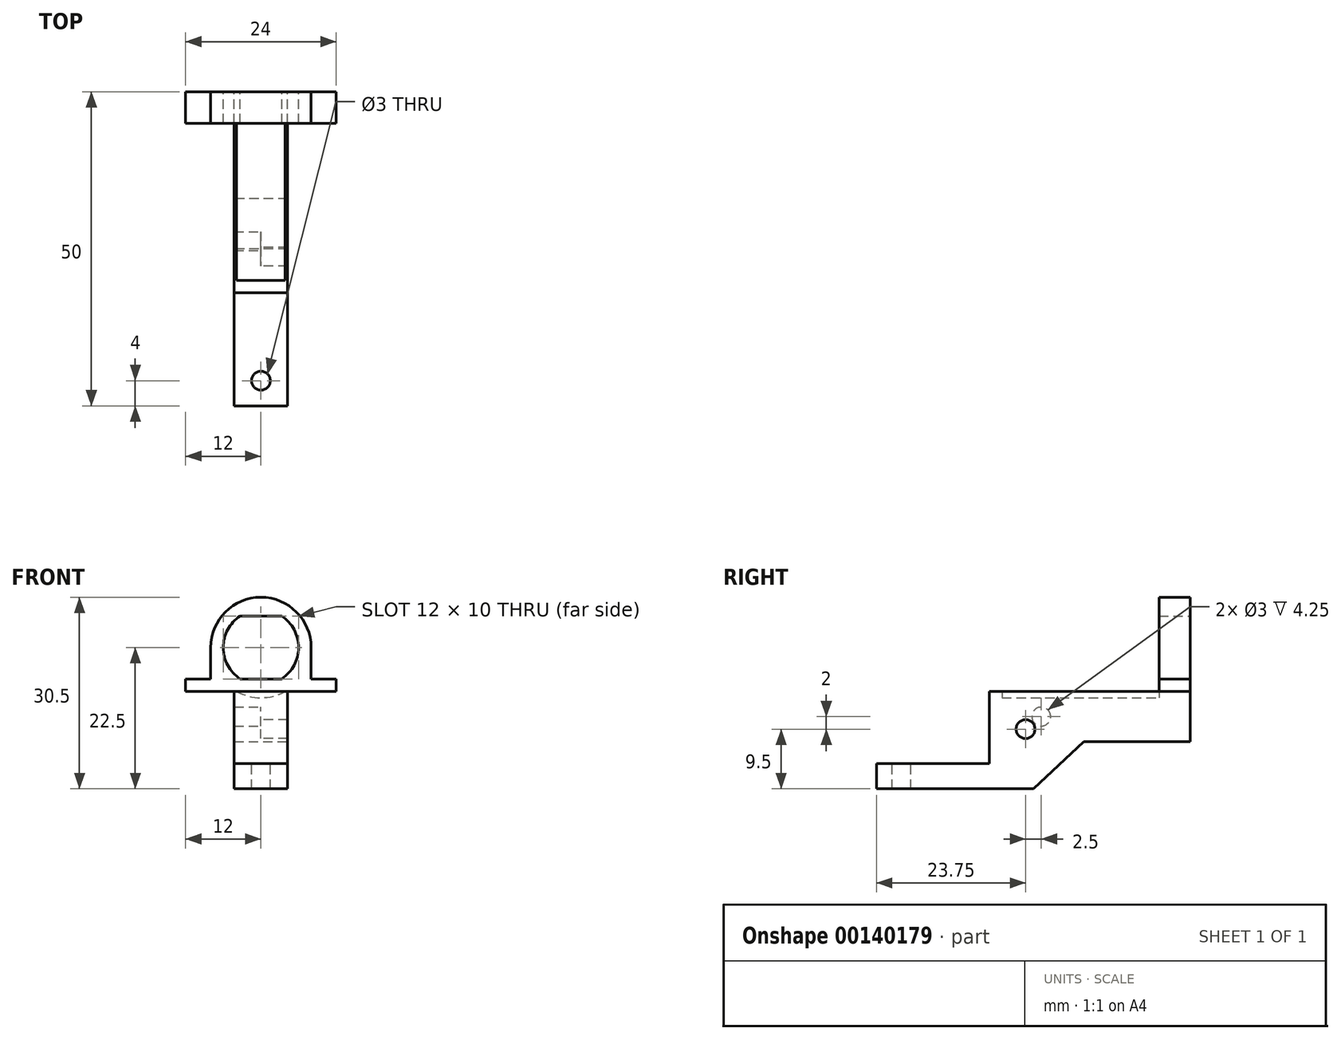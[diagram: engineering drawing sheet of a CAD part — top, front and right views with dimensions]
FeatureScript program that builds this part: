
annotation { "Feature Type Name" : "Feature", "Feature Type Description" : "" }
export const myFeature = defineFeature(function(context is Context, id is Id, definition is map)
    precondition{}
    {
        {
            var Q0;
            Q0=qCreatedBy(makeId("Front.planeOp"),FACE);
            var sketch = newSketch(context, id + "F0", { "sketchPlane" : qUnion([Q0])});
            skArc(sketch, "E0", {"start": v(3.32, 2) * mm, "mid": v(6, 7) * mm, "end": v(3.32, 12) * mm});
            skLineSegment(sketch, "E1", {"start": v(-3.32, 12) * mm, "end": v(3.32, 12) * mm});
            skLineSegment(sketch, "E2", {"start": v(-3.32, 2) * mm, "end": v(3.32, 2) * mm});
            skLineSegment(sketch, "E3", {"start": v(-8, 2) * mm, "end": v(-12, 2) * mm});
            skLineSegment(sketch, "E4", {"start": v(-12, 2) * mm, "end": v(-12, 0) * mm});
            skLineSegment(sketch, "E5", {"start": v(-12, 0) * mm, "end": v(0, 0) * mm});
            skArc(sketch, "E6.trimOffspring", {"start": v(-3.32, 12) * mm, "mid": v(-6, 7) * mm, "end": v(-3.32, 2) * mm});
            skArc(sketch, "E7", {"start": v(8, 7) * mm, "mid": v(0, 15) * mm, "end": v(-8, 7) * mm});
            skLineSegment(sketch, "E8", {"start": v(-8, 7) * mm, "end": v(-8, 2) * mm});
            skLineSegment(sketch, "E9.MirrorCS", {"start": v(8, 7) * mm, "end": v(8, 2) * mm});
            skLineSegment(sketch, "E10.MirrorCS", {"start": v(8, 2) * mm, "end": v(12, 2) * mm});
            skLineSegment(sketch, "E11.MirrorCS", {"start": v(12, 2) * mm, "end": v(12, 0) * mm});
            skLineSegment(sketch, "E12.MirrorCS", {"start": v(12, 0) * mm, "end": v(0, 0) * mm});
            skLineSegment(sketch, "E13.bottom", {"start": v(-4.25, 0) * mm, "end": v(4.25, 0) * mm});
            skLineSegment(sketch, "E13.top", {"start": v(-4.25, -8) * mm, "end": v(4.25, -8) * mm});
            skLineSegment(sketch, "E13.left", {"start": v(-4.25, 0) * mm, "end": v(-4.25, -8) * mm});
            skLineSegment(sketch, "E13.right", {"start": v(4.25, 0) * mm, "end": v(4.25, -8) * mm});
            skSolve(sketch);
        }
        {
            var Q0;
            Q0=makeQuery(id+"F0.imprint","IMPRINT",FACE,{"disambiguationData":[TD([[makeQuery(id+"F0.imprint","IMPRINT",EDGE,{"derivedFrom":sQuery(id+"F0.wireOp",EDGE,"E0")}),-1.0]])]});
            extrude(context, id + "F1", {"entities" : qUnion([Q0]), "depth" : 5 * mm});
        }
        {
            var Q0;
            Q0=makeQuery(id+"F0.imprint","IMPRINT",FACE,{"disambiguationData":[TD([[makeQuery(id+"F0.imprint","IMPRINT",EDGE,{"derivedFrom":sQuery(id+"F0.wireOp",EDGE,"E13.top")}),1.0]])]});
            extrude(context, id + "F2", {"entities" : qUnion([Q0]), "operationType" : NewBodyOperationType.ADD, "depth" : 32 * mm});
        }
        {
            var Q0;
            Q0=qCreatedBy(makeId("Right.planeOp"),FACE);
            var sketch = newSketch(context, id + "F3", { "sketchPlane" : qUnion([Q0])});
            skCircle(sketch, "E14", {"center": v(-26.25, -6) * mm, "radius": 1.5 * mm});
            skCircle(sketch, "E15", {"center": v(-23.75, -4) * mm, "radius": 1.5 * mm});
            skSolve(sketch);
        }
        {
            var Q0;
            Q0=makeQuery(id+"F3.imprint","IMPRINT",FACE,{"disambiguationData":[TD([[makeQuery(id+"F3.imprint","IMPRINT",EDGE,{"derivedFrom":sQuery(id+"F3.wireOp",EDGE,"E15")}),1.0]])]});
            extrude(context, id + "F4", {"entities" : qUnion([Q0]), "operationType" : NewBodyOperationType.REMOVE, "oppositeDirection" : true, "depth" : 25 * mm});
        }
        {
            var Q0;
            Q0=makeQuery(id+"F3.imprint","IMPRINT",FACE,{"disambiguationData":[TD([[makeQuery(id+"F3.imprint","IMPRINT",EDGE,{"derivedFrom":sQuery(id+"F3.wireOp",EDGE,"E14")}),1.0]])]});
            extrude(context, id + "F5", {"entities" : qUnion([Q0]), "operationType" : NewBodyOperationType.REMOVE, "depth" : 25 * mm});
        }
        {
            var Q0;
            Q0=makeQuery(id+"F1.opExtrude","CAP_FACE",FACE,{"disambiguationData":[OSD([sQuery(id+"F0.wireOp",EDGE,"E0"),sQuery(id+"F0.wireOp",EDGE,"E1"),sQuery(id+"F0.wireOp",EDGE,"E2"),sQuery(id+"F0.wireOp",EDGE,"E3"),sQuery(id+"F0.wireOp",EDGE,"E4"),sQuery(id+"F0.wireOp",EDGE,"E5"),sQuery(id+"F0.wireOp",EDGE,"E6.trimOffspring"),sQuery(id+"F0.wireOp",EDGE,"E7"),sQuery(id+"F0.wireOp",EDGE,"E8"),sQuery(id+"F0.wireOp",EDGE,"E9.MirrorCS"),sQuery(id+"F0.wireOp",EDGE,"E10.MirrorCS"),sQuery(id+"F0.wireOp",EDGE,"E11.MirrorCS"),sQuery(id+"F0.wireOp",EDGE,"E12.MirrorCS"),sQuery(id+"F0.wireOp",EDGE,"E13.bottom")])],"isStart":false});
            var sketch = newSketch(context, id + "F6", { "sketchPlane" : qUnion([Q0])});
            skCircle(sketch, "E16", {"center": v(0, 7) * mm, "radius": 8 * mm});
            skSolve(sketch);
        }
        {
            var Q0;
            Q0 = qSketchRegion(id + "F6", true);
            extrude(context, id + "F7", {"entities" : qUnion([Q0]), "operationType" : NewBodyOperationType.REMOVE, "depth" : 25 * mm});
        }
        {
            var Q0;
            Q0=qCreatedBy(makeId("Right.planeOp"),FACE);
            var sketch = newSketch(context, id + "F8", { "sketchPlane" : qUnion([Q0])});
            skLineSegment(sketch, "E17.bottom", {"start": v(-32, -11.5) * mm, "end": v(-50, -11.5) * mm});
            skLineSegment(sketch, "E17.top", {"start": v(-25, -15.5) * mm, "end": v(-50, -15.5) * mm});
            skLineSegment(sketch, "E17.right", {"start": v(-50, -11.5) * mm, "end": v(-50, -15.5) * mm});
            skLineSegment(sketch, "E18", {"start": v(-32, -11.5) * mm, "end": v(-32, -8) * mm});
            skLineSegment(sketch, "E19", {"start": v(-32, -8) * mm, "end": v(-17, -8) * mm});
            skLineSegment(sketch, "E20", {"start": v(-17, -8) * mm, "end": v(-25, -15.5) * mm});
            skSolve(sketch);
        }
        {
            var Q0;
            Q0=makeQuery(id+"F8.imprint","IMPRINT",FACE,{"disambiguationData":[TD([[makeQuery(id+"F8.imprint","IMPRINT",EDGE,{"derivedFrom":sQuery(id+"F8.wireOp",EDGE,"E17.bottom")}),1.0]])]});
            extrude(context, id + "F9", {"entities" : qUnion([Q0]), "operationType" : NewBodyOperationType.ADD, "depth" : 4.25 * mm, "hasSecondDirection" : true, "secondDirectionOppositeDirection" : true, "secondDirectionDepth" : 4.25 * mm});
        }
        {
            var Q0;
            Q0=makeQuery(id+"F9.opExtrude","SWEPT_FACE",FACE,{"disambiguationData":[OSD([sQuery(id+"F8.wireOp",EDGE,"E17.bottom")])]});
            var sketch = newSketch(context, id + "F10", { "sketchPlane" : qUnion([Q0])});
            skCircle(sketch, "E21", {"center": v(0, -46) * mm, "radius": 1.5 * mm});
            skPoint(sketch, "E21.centerSnap0", {"position": v(0, -32) * mm});
            skSolve(sketch);
        }
        {
            var Q0;
            Q0 = qSketchRegion(id + "F10", true);
            extrude(context, id + "F11", {"entities" : qUnion([Q0]), "operationType" : NewBodyOperationType.REMOVE, "oppositeDirection" : true, "depth" : 25 * mm});
        }
    });
